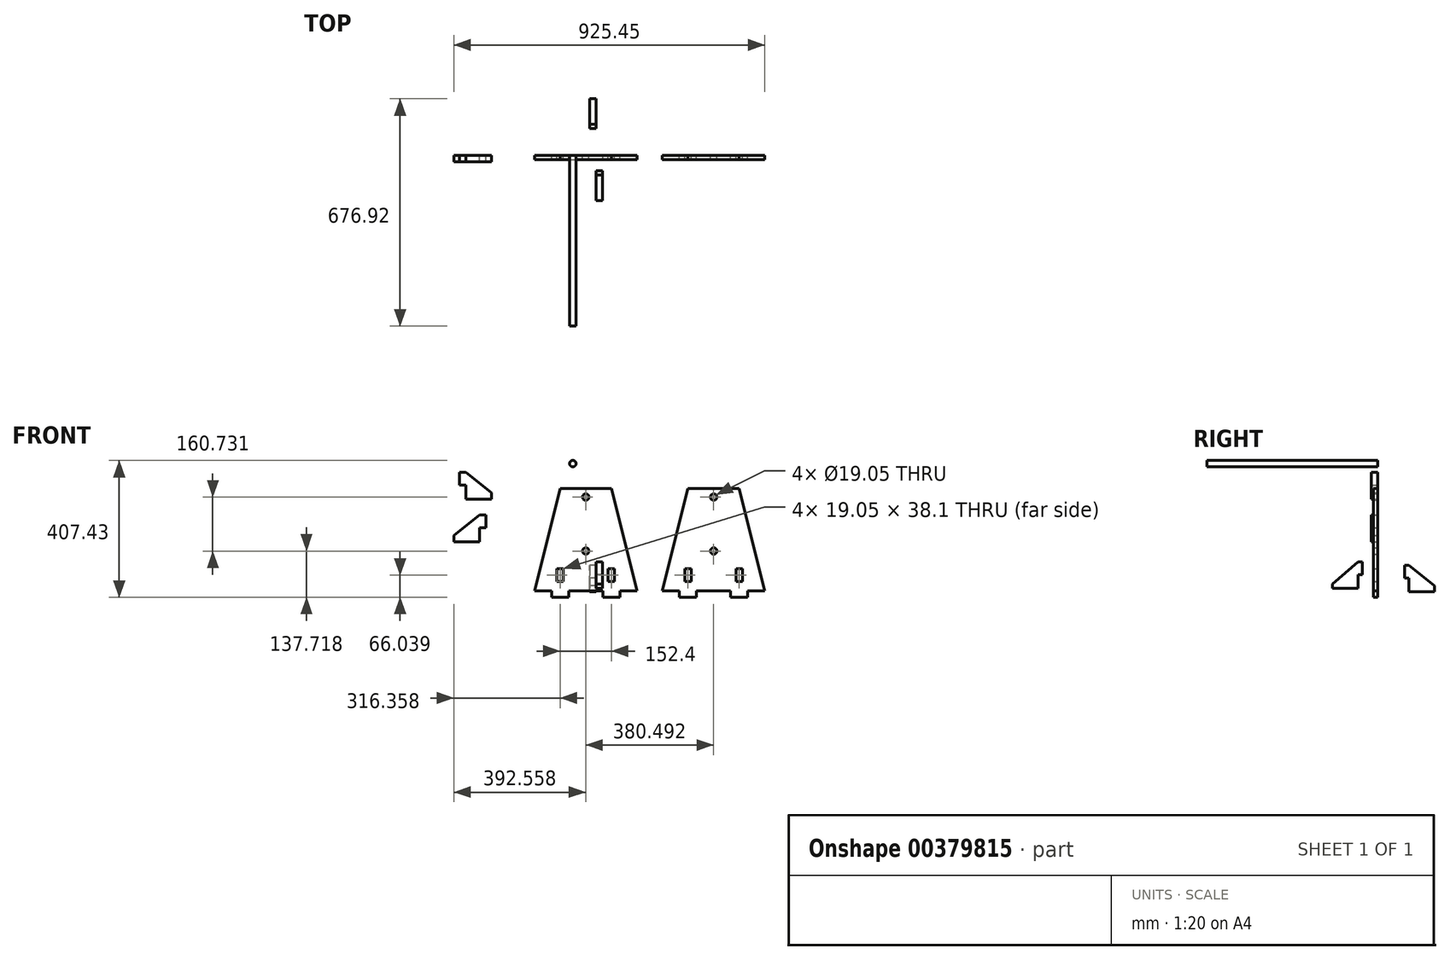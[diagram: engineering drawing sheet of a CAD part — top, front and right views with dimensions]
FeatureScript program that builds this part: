
annotation { "Feature Type Name" : "Feature", "Feature Type Description" : "" }
export const myFeature = defineFeature(function(context is Context, id is Id, definition is map)
    precondition{}
    {
        {
            var Q0;
            Q0=qCreatedBy(makeId("Front.planeOp"),FACE);
            var sketch = newSketch(context, id + "F0", { "sketchPlane" : qUnion([Q0])});
            skLineSegment(sketch, "E0", {"start": v(-87.7, -51.7) * mm, "end": v(64.7, -51.7) * mm});
            skLineSegment(sketch, "E1", {"start": v(-11.5, -51.7) * mm, "end": v(-11.5, -356.5) * mm, "construction": true});
            skLineSegment(sketch, "E2", {"start": v(-11.5, -356.5) * mm, "end": v(-163.9, -356.5) * mm});
            skLineSegment(sketch, "E3", {"start": v(-11.5, -356.5) * mm, "end": v(140.9, -356.5) * mm});
            skLineSegment(sketch, "E4", {"start": v(-87.7, -51.7) * mm, "end": v(-163.9, -356.5) * mm});
            skLineSegment(sketch, "E5", {"start": v(64.7, -51.7) * mm, "end": v(140.9, -356.5) * mm});
            skCircle(sketch, "E6", {"center": v(-11.5, -77.1) * mm, "radius": 9.53 * mm});
            skCircle(sketch, "E7", {"center": v(-11.5, -237.82) * mm, "radius": 9.53 * mm});
            skLineSegment(sketch, "E8", {"start": v(-87.7, -51.7) * mm, "end": v(-87.7, -356.5) * mm, "construction": true});
            skLineSegment(sketch, "E9", {"start": v(64.7, -51.7) * mm, "end": v(64.7, -356.5) * mm, "construction": true});
            skPoint(sketch, "E10", {"position": v(-113.1, -356.5) * mm});
            skPoint(sketch, "E11", {"position": v(-62.3, -356.5) * mm});
            skPoint(sketch, "E12", {"position": v(39.3, -356.5) * mm});
            skPoint(sketch, "E13", {"position": v(90.1, -356.5) * mm});
            skLineSegment(sketch, "E14", {"start": v(-113.1, -356.5) * mm, "end": v(-113.1, -375.54) * mm});
            skLineSegment(sketch, "E15", {"start": v(-62.3, -356.5) * mm, "end": v(-62.3, -375.54) * mm});
            skLineSegment(sketch, "E16", {"start": v(-113.1, -375.54) * mm, "end": v(-62.3, -375.54) * mm});
            skLineSegment(sketch, "E17", {"start": v(39.3, -356.5) * mm, "end": v(39.3, -375.54) * mm});
            skLineSegment(sketch, "E18", {"start": v(90.1, -356.5) * mm, "end": v(90.1, -375.54) * mm});
            skLineSegment(sketch, "E19", {"start": v(39.3, -375.54) * mm, "end": v(90.1, -375.54) * mm});
            skPoint(sketch, "E20", {"position": v(64.7, -290.45) * mm});
            skPoint(sketch, "E21", {"position": v(64.7, -328.55) * mm});
            skLineSegment(sketch, "E22", {"start": v(64.7, -290.45) * mm, "end": v(74.22, -290.45) * mm});
            skLineSegment(sketch, "E23", {"start": v(74.22, -290.45) * mm, "end": v(74.22, -328.55) * mm});
            skLineSegment(sketch, "E24", {"start": v(74.22, -328.55) * mm, "end": v(64.7, -328.55) * mm});
            skLineSegment(sketch, "E25", {"start": v(64.7, -328.55) * mm, "end": v(55.17, -328.55) * mm});
            skLineSegment(sketch, "E26", {"start": v(55.17, -328.55) * mm, "end": v(55.17, -290.45) * mm});
            skLineSegment(sketch, "E27", {"start": v(64.7, -290.45) * mm, "end": v(55.17, -290.45) * mm});
            skLineSegment(sketch, "E28.MirrorCS", {"start": v(-87.7, -290.45) * mm, "end": v(-78.18, -290.45) * mm});
            skLineSegment(sketch, "E29.MirrorCS", {"start": v(-78.18, -328.55) * mm, "end": v(-78.18, -290.45) * mm});
            skLineSegment(sketch, "E30.MirrorCS", {"start": v(-87.7, -328.55) * mm, "end": v(-78.18, -328.55) * mm});
            skLineSegment(sketch, "E31.MirrorCS", {"start": v(-97.23, -328.55) * mm, "end": v(-87.7, -328.55) * mm});
            skLineSegment(sketch, "E32.MirrorCS", {"start": v(-97.23, -290.45) * mm, "end": v(-97.23, -328.55) * mm});
            skLineSegment(sketch, "E33.MirrorCS", {"start": v(-87.7, -290.45) * mm, "end": v(-97.23, -290.45) * mm});
            skSolve(sketch);
        }
        {
            var Q0;
            Q0 = qSketchRegion(id + "F0", true);
            extrude(context, id + "F1", {"entities" : qUnion([Q0]), "depth" : 12.7 * mm});
        }
        {
            var Q0;
            Q0=makeQuery(id+"F1.opExtrude","SWEPT_BODY",BODY,{"disambiguationData":[OSD([sQuery(id+"F0.wireOp",EDGE,"E0"),sQuery(id+"F0.wireOp",EDGE,"E2"),sQuery(id+"F0.wireOp",EDGE,"E3"),sQuery(id+"F0.wireOp",EDGE,"E4"),sQuery(id+"F0.wireOp",EDGE,"E5"),sQuery(id+"F0.wireOp",EDGE,"E6")])]});
            transform(context, id + "F2", {"entities" : qUnion([Q0]), "transformType" : TransformType.TRANSLATION_3D, "dx" : 380.5 * mm, "dy" : 0 * mm, "dz" : 0 * mm, "makeCopy" : true});
        }
        {
            var Q0;
            Q0=qCreatedBy(makeId("Front.planeOp"),FACE);
            var sketch = newSketch(context, id + "F3", { "sketchPlane" : qUnion([Q0])});
            skCircle(sketch, "E34", {"center": v(-50.01, 22.37) * mm, "radius": 9.53 * mm});
            skSolve(sketch);
        }
        {
            var Q0;
            Q0=makeQuery(id+"F3.imprint","IMPRINT",FACE,{"disambiguationData":[TD([[makeQuery(id+"F3.imprint","IMPRINT",EDGE,{"derivedFrom":sQuery(id+"F3.wireOp",EDGE,"E34")}),1.0]])]});
            extrude(context, id + "F4", {"entities" : qUnion([Q0]), "depth" : 508 * mm});
        }
        {
            var Q0;
            Q0=qCreatedBy(makeId("Right.planeOp"),FACE);
            var sketch = newSketch(context, id + "F5", { "sketchPlane" : qUnion([Q0])});
            skLineSegment(sketch, "E35", {"start": v(92.72, -280.5) * mm, "end": v(92.72, -341.46) * mm});
            skLineSegment(sketch, "E36", {"start": v(92.72, -341.46) * mm, "end": v(168.92, -341.46) * mm});
            skLineSegment(sketch, "E37", {"start": v(168.92, -341.46) * mm, "end": v(92.72, -280.5) * mm});
            skLineSegment(sketch, "E38", {"start": v(92.72, -341.46) * mm, "end": v(92.72, -359.24) * mm});
            skLineSegment(sketch, "E39", {"start": v(92.72, -359.24) * mm, "end": v(168.92, -359.24) * mm});
            skLineSegment(sketch, "E40", {"start": v(168.92, -359.24) * mm, "end": v(168.92, -341.46) * mm});
            skLineSegment(sketch, "E41", {"start": v(92.72, -280.5) * mm, "end": v(80.02, -280.5) * mm});
            skLineSegment(sketch, "E42", {"start": v(80.02, -280.5) * mm, "end": v(80.02, -318.6) * mm});
            skLineSegment(sketch, "E43", {"start": v(80.02, -318.6) * mm, "end": v(92.72, -318.6) * mm});
            skSolve(sketch);
        }
        {
            var Q0;
            Q0=makeQuery(id+"F5.imprint","IMPRINT",FACE,{"disambiguationData":[TD([[makeQuery(id+"F5.imprint","IMPRINT",EDGE,{"derivedFrom":sQuery(id+"F5.wireOp",EDGE,"E35")}),1.0]])]});
            var Q1;
            Q1=makeQuery(id+"F5.imprint","IMPRINT",FACE,{"disambiguationData":[TD([[makeQuery(id+"F5.imprint","IMPRINT",EDGE,{"derivedFrom":sQuery(id+"F5.wireOp",EDGE,"E36")}),-1.0]])]});
            var Q2;
            {var subQ0=sQuery(id+"F5.wireOp",EDGE,"E41");Q2=makeQuery(id+"F5.imprint","IMPRINT",FACE,{"disambiguationData":[TD([[makeQuery(id+"F5.imprint","IMPRINT",EDGE,{"derivedFrom":subQ0}),1.0]])]});}
            extrude(context, id + "F6", {"entities" : qUnion([Q0, Q1, Q2]), "depth" : 19.05 * mm});
        }
        {
            var Q0;
            Q0=makeQuery(id+"F6.opExtrude","CAP_FACE",FACE,{"disambiguationData":[OSD([sQuery(id+"F5.wireOp",EDGE,"E35"),sQuery(id+"F5.wireOp",EDGE,"E36"),sQuery(id+"F5.wireOp",EDGE,"E37")])],"isStart":false});
            var sketch = newSketch(context, id + "F7", { "sketchPlane" : qUnion([Q0])});
            skLineSegment(sketch, "E44", {"start": v(-134.68, -336.62) * mm, "end": v(-58.48, -270.58) * mm});
            skLineSegment(sketch, "E45", {"start": v(-58.48, -270.58) * mm, "end": v(-58.48, -349.32) * mm});
            skLineSegment(sketch, "E46", {"start": v(-134.68, -336.62) * mm, "end": v(-58.48, -336.62) * mm});
            skLineSegment(sketch, "E47", {"start": v(-134.68, -349.32) * mm, "end": v(-134.68, -336.62) * mm});
            skLineSegment(sketch, "E48", {"start": v(-134.68, -349.32) * mm, "end": v(-58.48, -349.32) * mm});
            skLineSegment(sketch, "E49", {"start": v(-58.48, -270.58) * mm, "end": v(-45.78, -270.58) * mm});
            skLineSegment(sketch, "E50", {"start": v(-45.78, -270.58) * mm, "end": v(-45.78, -308.68) * mm});
            skLineSegment(sketch, "E51", {"start": v(-45.78, -308.68) * mm, "end": v(-58.48, -308.68) * mm});
            skSolve(sketch);
        }
        {
            var Q0;
            {var subQ0=sQuery(id+"F7.wireOp",EDGE,"E44");Q0=makeQuery(id+"F7.imprint","IMPRINT",FACE,{"disambiguationData":[TD([[makeQuery(id+"F7.imprint","IMPRINT",EDGE,{"derivedFrom":subQ0}),-1.0]])]});}
            var Q1;
            {var subQ2=sQuery(id+"F7.wireOp",EDGE,"E46");Q1=makeQuery(id+"F7.imprint","IMPRINT",FACE,{"disambiguationData":[TD([[makeQuery(id+"F7.imprint","IMPRINT",EDGE,{"derivedFrom":subQ2}),-1.0]])]});}
            var Q2;
            {var subQ0=sQuery(id+"F7.wireOp",EDGE,"E49");Q2=makeQuery(id+"F7.imprint","IMPRINT",FACE,{"disambiguationData":[TD([[makeQuery(id+"F7.imprint","IMPRINT",EDGE,{"derivedFrom":subQ0}),-1.0]])]});}
            extrude(context, id + "F8", {"entities" : qUnion([Q0, Q1, Q2]), "depth" : 19.05 * mm});
        }
        {
            var Q0;
            Q0=qCreatedBy(makeId("Front.planeOp"),FACE);
            var sketch = newSketch(context, id + "F9", { "sketchPlane" : qUnion([Q0])});
            skLineSegment(sketch, "E52", {"start": v(-367.54, -3.48) * mm, "end": v(-367.54, -64.44) * mm});
            skLineSegment(sketch, "E53", {"start": v(-367.54, -64.44) * mm, "end": v(-291.34, -64.44) * mm});
            skLineSegment(sketch, "E54", {"start": v(-291.34, -64.44) * mm, "end": v(-367.54, -3.48) * mm});
            skLineSegment(sketch, "E55", {"start": v(-367.54, -64.44) * mm, "end": v(-367.54, -83.5) * mm});
            skLineSegment(sketch, "E56", {"start": v(-367.54, -83.5) * mm, "end": v(-291.34, -83.5) * mm});
            skLineSegment(sketch, "E57", {"start": v(-291.34, -83.5) * mm, "end": v(-291.34, -64.44) * mm});
            skLineSegment(sketch, "E58", {"start": v(-367.54, -3.48) * mm, "end": v(-386.59, -3.48) * mm});
            skLineSegment(sketch, "E59", {"start": v(-386.59, -3.48) * mm, "end": v(-386.59, -41.58) * mm});
            skLineSegment(sketch, "E60", {"start": v(-386.59, -41.58) * mm, "end": v(-367.54, -41.58) * mm});
            skLineSegment(sketch, "E61", {"start": v(-404.06, -191.92) * mm, "end": v(-327.86, -130.96) * mm});
            skLineSegment(sketch, "E62", {"start": v(-327.86, -130.96) * mm, "end": v(-327.86, -210.97) * mm});
            skLineSegment(sketch, "E63", {"start": v(-404.06, -191.92) * mm, "end": v(-327.86, -191.92) * mm});
            skLineSegment(sketch, "E64", {"start": v(-404.06, -210.97) * mm, "end": v(-404.06, -191.92) * mm});
            skLineSegment(sketch, "E65", {"start": v(-404.06, -210.97) * mm, "end": v(-327.86, -210.97) * mm});
            skLineSegment(sketch, "E66", {"start": v(-327.86, -130.96) * mm, "end": v(-308.8, -130.96) * mm});
            skLineSegment(sketch, "E67", {"start": v(-308.8, -130.96) * mm, "end": v(-308.8, -169.06) * mm});
            skLineSegment(sketch, "E68", {"start": v(-308.8, -169.06) * mm, "end": v(-327.86, -169.06) * mm});
            skSolve(sketch);
        }
        {
            var Q0;
            Q0 = qSketchRegion(id + "F9", true);
            extrude(context, id + "F10", {"entities" : qUnion([Q0]), "depth" : 19.05 * mm});
        }
    });
